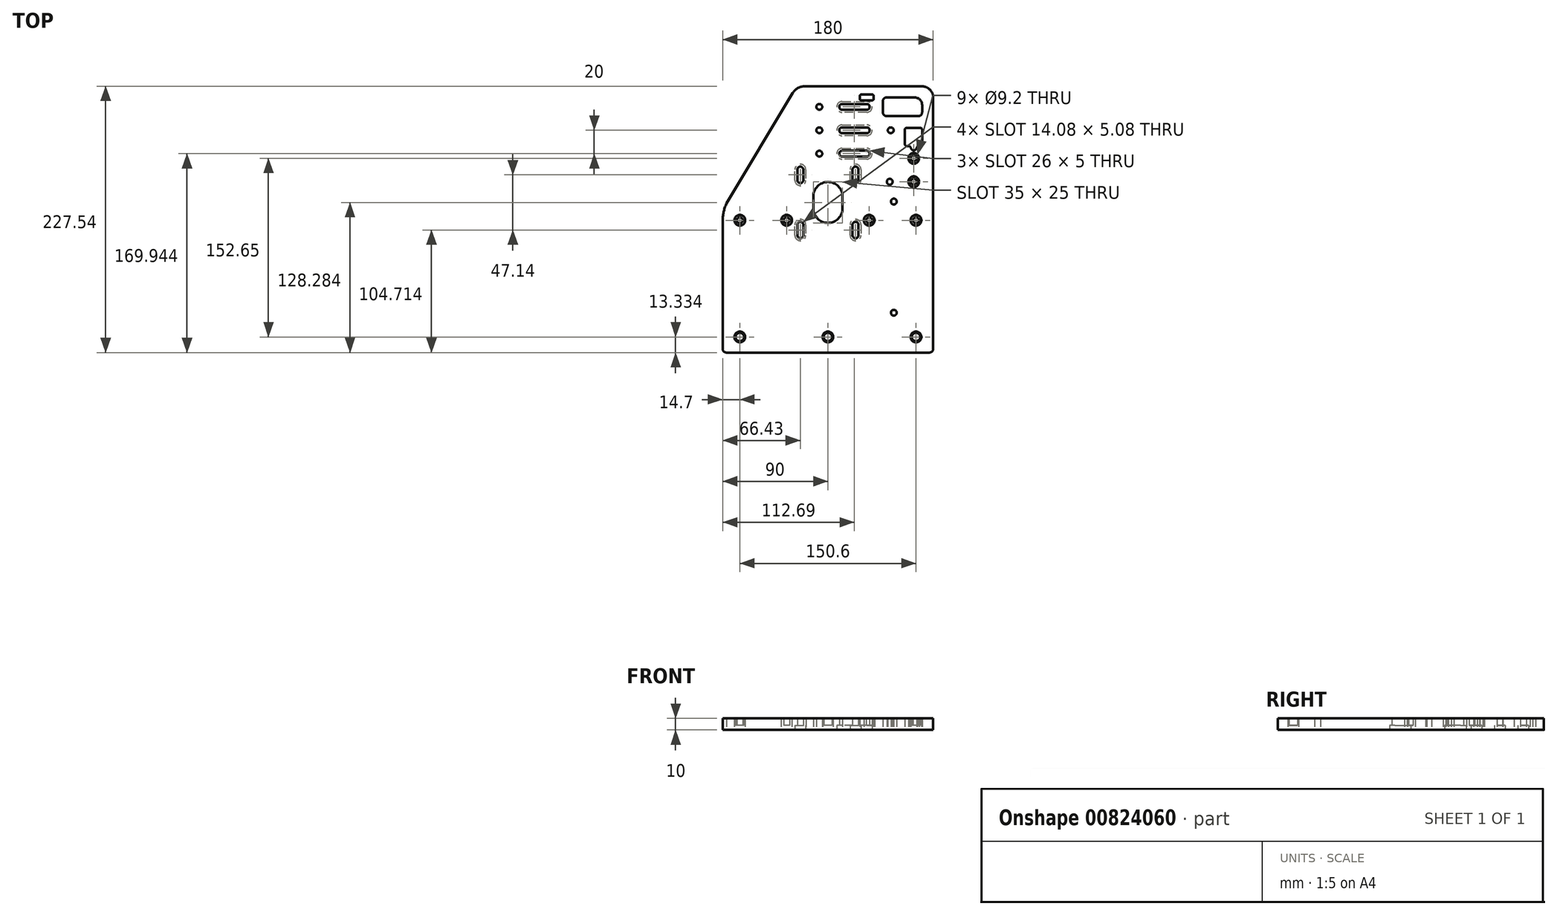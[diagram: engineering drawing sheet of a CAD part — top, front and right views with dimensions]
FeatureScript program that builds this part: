
annotation { "Feature Type Name" : "Feature", "Feature Type Description" : "" }
export const myFeature = defineFeature(function(context is Context, id is Id, definition is map)
    precondition{}
    {
        {
            var Q0;
            Q0=qCreatedBy(makeId("Top.planeOp"),FACE);
            var sketch = newSketch(context, id + "F0", { "sketchPlane" : qUnion([Q0])});
            skLineSegment(sketch, "E0", {"start": v(-86.67, -113.77) * mm, "end": v(86.64, -113.77) * mm});
            skLineSegment(sketch, "E1", {"start": v(-90, -1.46) * mm, "end": v(-90, -110.4) * mm});
            skLineSegment(sketch, "E2", {"start": v(-30.03, 107.94) * mm, "end": v(-86.68, 13.65) * mm});
            skLineSegment(sketch, "E3", {"start": v(-26.11, -13.56) * mm, "end": v(-26.11, -4.56) * mm});
            skLineSegment(sketch, "E4", {"start": v(-26.11, 33.58) * mm, "end": v(-26.11, 42.58) * mm});
            skLineSegment(sketch, "E5", {"start": v(-21.03, 42.58) * mm, "end": v(-21.03, 33.58) * mm});
            skLineSegment(sketch, "E6", {"start": v(-21.03, -4.56) * mm, "end": v(-21.03, -13.56) * mm});
            skLineSegment(sketch, "E7", {"start": v(-12.5, 9.51) * mm, "end": v(-12.5, 19.51) * mm});
            skLineSegment(sketch, "E8", {"start": v(12.5, 19.51) * mm, "end": v(12.5, 9.51) * mm});
            skLineSegment(sketch, "E9", {"start": v(21.03, -13.56) * mm, "end": v(21.03, -4.56) * mm});
            skLineSegment(sketch, "E10", {"start": v(21.03, 33.58) * mm, "end": v(21.03, 42.58) * mm});
            skLineSegment(sketch, "E11", {"start": v(26.1, 42.58) * mm, "end": v(26.1, 33.58) * mm});
            skLineSegment(sketch, "E12", {"start": v(26.1, -4.56) * mm, "end": v(26.1, -13.56) * mm});
            skLineSegment(sketch, "E13", {"start": v(27.19, 103.2) * mm, "end": v(27.19, 105.32) * mm});
            skLineSegment(sketch, "E14", {"start": v(76.37, 62.2) * mm, "end": v(75.8, 61.48) * mm});
            skLineSegment(sketch, "E15", {"start": v(39.19, 105.32) * mm, "end": v(39.19, 103.2) * mm});
            skLineSegment(sketch, "E16", {"start": v(47, 91.4) * mm, "end": v(47, 101.1) * mm});
            skLineSegment(sketch, "E17", {"start": v(33.19, 53.67) * mm, "end": v(12.19, 53.67) * mm});
            skLineSegment(sketch, "E18", {"start": v(12.19, 58.67) * mm, "end": v(33.19, 58.67) * mm});
            skLineSegment(sketch, "E19", {"start": v(65.8, 64.35) * mm, "end": v(65.8, 76.68) * mm});
            skLineSegment(sketch, "E20", {"start": v(78.84, 62.2) * mm, "end": v(76.37, 62.2) * mm});
            skLineSegment(sketch, "E21", {"start": v(69.93, 62.7) * mm, "end": v(67.46, 62.7) * mm});
            skLineSegment(sketch, "E22", {"start": v(33.19, 73.67) * mm, "end": v(12.19, 73.67) * mm});
            skLineSegment(sketch, "E23", {"start": v(67.46, 78.34) * mm, "end": v(78.84, 78.34) * mm});
            skLineSegment(sketch, "E24", {"start": v(80.5, 97.88) * mm, "end": v(80.5, 91.4) * mm});
            skLineSegment(sketch, "E25", {"start": v(80.5, 76.68) * mm, "end": v(80.5, 63.85) * mm});
            skLineSegment(sketch, "E26", {"start": v(12.19, 78.67) * mm, "end": v(33.19, 78.67) * mm});
            skLineSegment(sketch, "E27", {"start": v(77.36, 88.26) * mm, "end": v(50.14, 88.26) * mm});
            skLineSegment(sketch, "E28", {"start": v(90, -110.4) * mm, "end": v(90, 104.05) * mm});
            skLineSegment(sketch, "E29", {"start": v(33.19, 93.67) * mm, "end": v(12.19, 93.67) * mm});
            skLineSegment(sketch, "E30", {"start": v(70.9, 61.48) * mm, "end": v(69.93, 62.7) * mm});
            skLineSegment(sketch, "E31", {"start": v(12.19, 98.67) * mm, "end": v(33.19, 98.67) * mm});
            skLineSegment(sketch, "E32", {"start": v(37.75, 101.76) * mm, "end": v(28.63, 101.76) * mm});
            skLineSegment(sketch, "E33", {"start": v(50.14, 104.23) * mm, "end": v(74.15, 104.23) * mm});
            skLineSegment(sketch, "E34", {"start": v(28.63, 106.76) * mm, "end": v(37.75, 106.76) * mm});
            skLineSegment(sketch, "E35", {"start": v(80.33, 113.73) * mm, "end": v(-18.85, 113.73) * mm});
            skCircle(sketch, "E36", {"center": v(-75.3, -100.44) * mm, "radius": 3.6 * mm});
            skArc(sketch, "E37", {"start": v(-90, -110.4) * mm, "mid": v(-89.03, -112.77) * mm, "end": v(-86.67, -113.77) * mm});
            skArc(sketch, "E38", {"start": v(-26.11, -13.56) * mm, "mid": v(-23.57, -16.1) * mm, "end": v(-21.03, -13.56) * mm});
            skArc(sketch, "E39", {"start": v(-21.03, -4.56) * mm, "mid": v(-23.57, -2.02) * mm, "end": v(-26.11, -4.56) * mm});
            skArc(sketch, "E40", {"start": v(-86.68, 13.65) * mm, "mid": v(-89.16, 6.28) * mm, "end": v(-90, -1.46) * mm});
            skArc(sketch, "E41", {"start": v(-18.85, 113.73) * mm, "mid": v(-25.26, 112.42) * mm, "end": v(-30.03, 107.94) * mm});
            skArc(sketch, "E42", {"start": v(-21.03, 42.58) * mm, "mid": v(-23.57, 45.12) * mm, "end": v(-26.11, 42.58) * mm});
            skArc(sketch, "E43", {"start": v(-26.11, 33.58) * mm, "mid": v(-23.57, 31.04) * mm, "end": v(-21.03, 33.58) * mm});
            skCircle(sketch, "E44", {"center": v(-7.31, 96.17) * mm, "radius": 2.5 * mm});
            skCircle(sketch, "E45", {"center": v(-7.31, 76.17) * mm, "radius": 2.5 * mm});
            skCircle(sketch, "E46", {"center": v(-7.31, 56.17) * mm, "radius": 2.5 * mm});
            skCircle(sketch, "E47", {"center": v(-35.3, -0.74) * mm, "radius": 2.5 * mm});
            skCircle(sketch, "E48", {"center": v(-75.3, -0.74) * mm, "radius": 2.5 * mm});
            skCircle(sketch, "E49", {"center": v(75.3, -100.44) * mm, "radius": 3.6 * mm});
            skCircle(sketch, "E50", {"center": v(0, -100.44) * mm, "radius": 3.6 * mm});
            skArc(sketch, "E51", {"start": v(86.64, -113.77) * mm, "mid": v(89.02, -112.78) * mm, "end": v(90, -110.4) * mm});
            skArc(sketch, "E52", {"start": v(21.03, -13.56) * mm, "mid": v(23.57, -16.1) * mm, "end": v(26.1, -13.56) * mm});
            skArc(sketch, "E53", {"start": v(26.1, -4.56) * mm, "mid": v(23.57, -2.02) * mm, "end": v(21.03, -4.56) * mm});
            skCircle(sketch, "E54", {"center": v(56.34, -79.74) * mm, "radius": 2.5 * mm});
            skArc(sketch, "E55", {"start": v(-12.5, 9.51) * mm, "mid": v(0, -2.99) * mm, "end": v(12.5, 9.51) * mm});
            skArc(sketch, "E56", {"start": v(12.5, 19.51) * mm, "mid": v(0, 32.01) * mm, "end": v(-12.5, 19.51) * mm});
            skArc(sketch, "E57", {"start": v(90, 104.05) * mm, "mid": v(87.17, 110.9) * mm, "end": v(80.33, 113.73) * mm});
            skArc(sketch, "E58", {"start": v(80.5, 97.88) * mm, "mid": v(78.64, 102.37) * mm, "end": v(74.15, 104.23) * mm});
            skArc(sketch, "E59", {"start": v(77.36, 88.26) * mm, "mid": v(79.58, 89.18) * mm, "end": v(80.5, 91.4) * mm});
            skArc(sketch, "E60", {"start": v(47, 91.4) * mm, "mid": v(47.92, 89.18) * mm, "end": v(50.14, 88.26) * mm});
            skArc(sketch, "E61", {"start": v(50.14, 104.23) * mm, "mid": v(47.92, 103.31) * mm, "end": v(47, 101.1) * mm});
            skArc(sketch, "E62", {"start": v(21.03, 33.58) * mm, "mid": v(23.57, 31.04) * mm, "end": v(26.1, 33.58) * mm});
            skArc(sketch, "E63", {"start": v(26.1, 42.58) * mm, "mid": v(23.57, 45.12) * mm, "end": v(21.03, 42.58) * mm});
            skArc(sketch, "E64", {"start": v(33.19, 93.67) * mm, "mid": v(35.69, 96.17) * mm, "end": v(33.19, 98.67) * mm});
            skArc(sketch, "E65", {"start": v(12.19, 98.67) * mm, "mid": v(9.69, 96.17) * mm, "end": v(12.19, 93.67) * mm});
            skArc(sketch, "E66", {"start": v(33.19, 73.67) * mm, "mid": v(35.69, 76.17) * mm, "end": v(33.19, 78.67) * mm});
            skArc(sketch, "E67", {"start": v(12.19, 78.67) * mm, "mid": v(9.69, 76.17) * mm, "end": v(12.19, 73.67) * mm});
            skArc(sketch, "E68", {"start": v(33.19, 53.67) * mm, "mid": v(35.69, 56.17) * mm, "end": v(33.19, 58.67) * mm});
            skArc(sketch, "E69", {"start": v(12.19, 58.67) * mm, "mid": v(9.69, 56.17) * mm, "end": v(12.19, 53.67) * mm});
            skCircle(sketch, "E70", {"center": v(53.69, 76.17) * mm, "radius": 2.5 * mm});
            skCircle(sketch, "E71", {"center": v(73.35, 52.21) * mm, "radius": 2.5 * mm});
            skCircle(sketch, "E72", {"center": v(73.35, 32.21) * mm, "radius": 2.5 * mm});
            skCircle(sketch, "E73", {"center": v(52.85, 32.21) * mm, "radius": 2.5 * mm});
            skCircle(sketch, "E74", {"center": v(56.34, 15.26) * mm, "radius": 2.5 * mm});
            skCircle(sketch, "E75", {"center": v(75.3, -0.74) * mm, "radius": 2.5 * mm});
            skCircle(sketch, "E76", {"center": v(35.3, -0.74) * mm, "radius": 2.5 * mm});
            skArc(sketch, "E77", {"start": v(80.5, 76.68) * mm, "mid": v(80.01, 77.86) * mm, "end": v(78.84, 78.34) * mm});
            skArc(sketch, "E78", {"start": v(78.84, 62.2) * mm, "mid": v(80.01, 62.68) * mm, "end": v(80.5, 63.85) * mm});
            skArc(sketch, "E79", {"start": v(65.8, 64.35) * mm, "mid": v(66.29, 63.18) * mm, "end": v(67.46, 62.7) * mm});
            skArc(sketch, "E80", {"start": v(67.46, 78.34) * mm, "mid": v(66.29, 77.86) * mm, "end": v(65.8, 76.68) * mm});
            skArc(sketch, "E81", {"start": v(39.19, 105.32) * mm, "mid": v(38.77, 106.34) * mm, "end": v(37.75, 106.76) * mm});
            skArc(sketch, "E82", {"start": v(37.75, 101.76) * mm, "mid": v(38.77, 102.19) * mm, "end": v(39.19, 103.2) * mm});
            skArc(sketch, "E83", {"start": v(27.19, 103.2) * mm, "mid": v(27.61, 102.19) * mm, "end": v(28.63, 101.76) * mm});
            skArc(sketch, "E84", {"start": v(28.63, 106.76) * mm, "mid": v(27.61, 106.34) * mm, "end": v(27.19, 105.32) * mm});
            skEllipticalArc(sketch, "E85", {});
            skArc(sketch, "E86.0", {"start": v(-28.21, -13.56) * mm, "mid": v(-23.57, -18.2) * mm, "end": v(-18.93, -13.56) * mm});
            skLineSegment(sketch, "E86.1", {"start": v(-28.21, -13.56) * mm, "end": v(-28.21, -4.56) * mm});
            skArc(sketch, "E86.2", {"start": v(-18.93, -4.56) * mm, "mid": v(-23.57, 0.08) * mm, "end": v(-28.21, -4.56) * mm});
            skLineSegment(sketch, "E86.3", {"start": v(-18.93, -4.56) * mm, "end": v(-18.93, -13.56) * mm});
            skArc(sketch, "E87.0", {"start": v(-18.93, 42.58) * mm, "mid": v(-23.57, 47.22) * mm, "end": v(-28.21, 42.58) * mm});
            skLineSegment(sketch, "E87.1", {"start": v(-18.93, 42.58) * mm, "end": v(-18.93, 33.58) * mm});
            skArc(sketch, "E87.2", {"start": v(-28.21, 33.58) * mm, "mid": v(-23.57, 28.94) * mm, "end": v(-18.93, 33.58) * mm});
            skLineSegment(sketch, "E87.3", {"start": v(-28.21, 33.58) * mm, "end": v(-28.21, 42.58) * mm});
            skArc(sketch, "E88.0", {"start": v(18.93, 33.58) * mm, "mid": v(23.57, 28.94) * mm, "end": v(28.2, 33.58) * mm});
            skLineSegment(sketch, "E88.1", {"start": v(18.93, 33.58) * mm, "end": v(18.93, 42.58) * mm});
            skArc(sketch, "E88.2", {"start": v(28.2, 42.58) * mm, "mid": v(23.57, 47.22) * mm, "end": v(18.93, 42.58) * mm});
            skLineSegment(sketch, "E88.3", {"start": v(28.2, 42.58) * mm, "end": v(28.2, 33.58) * mm});
            skArc(sketch, "E89.0", {"start": v(28.2, -4.56) * mm, "mid": v(23.57, 0.08) * mm, "end": v(18.93, -4.56) * mm});
            skLineSegment(sketch, "E89.1", {"start": v(28.2, -4.56) * mm, "end": v(28.2, -13.56) * mm});
            skArc(sketch, "E89.2", {"start": v(18.93, -13.56) * mm, "mid": v(23.57, -18.2) * mm, "end": v(28.2, -13.56) * mm});
            skLineSegment(sketch, "E89.3", {"start": v(18.93, -13.56) * mm, "end": v(18.93, -4.56) * mm});
            skCircle(sketch, "E90.0", {"center": v(-75.3, -100.44) * mm, "radius": 4.6 * mm});
            skCircle(sketch, "E91.0", {"center": v(0, -100.44) * mm, "radius": 4.6 * mm});
            skCircle(sketch, "E92.0", {"center": v(75.3, -100.44) * mm, "radius": 4.6 * mm});
            skCircle(sketch, "E93.0", {"center": v(75.3, -0.74) * mm, "radius": 4.6 * mm});
            skCircle(sketch, "E94.0", {"center": v(35.3, -0.74) * mm, "radius": 4.6 * mm});
            skCircle(sketch, "E95.0", {"center": v(-35.3, -0.74) * mm, "radius": 4.6 * mm});
            skCircle(sketch, "E96.0", {"center": v(-75.3, -0.74) * mm, "radius": 4.6 * mm});
            skArc(sketch, "E97.0", {"start": v(12.19, 100.77) * mm, "mid": v(7.59, 96.17) * mm, "end": v(12.19, 91.57) * mm});
            skLineSegment(sketch, "E97.1", {"start": v(12.19, 100.77) * mm, "end": v(33.19, 100.77) * mm});
            skArc(sketch, "E97.2", {"start": v(33.19, 91.57) * mm, "mid": v(37.79, 96.17) * mm, "end": v(33.19, 100.77) * mm});
            skLineSegment(sketch, "E97.3", {"start": v(33.19, 91.57) * mm, "end": v(12.19, 91.57) * mm});
            skLineSegment(sketch, "E98.0", {"start": v(12.19, 80.77) * mm, "end": v(33.19, 80.77) * mm});
            skArc(sketch, "E98.1", {"start": v(12.19, 80.77) * mm, "mid": v(7.59, 76.17) * mm, "end": v(12.19, 71.57) * mm});
            skLineSegment(sketch, "E98.2", {"start": v(33.19, 71.57) * mm, "end": v(12.19, 71.57) * mm});
            skArc(sketch, "E98.3", {"start": v(33.19, 71.57) * mm, "mid": v(37.79, 76.17) * mm, "end": v(33.19, 80.77) * mm});
            skLineSegment(sketch, "E99.0", {"start": v(12.19, 60.77) * mm, "end": v(33.19, 60.77) * mm});
            skArc(sketch, "E99.1", {"start": v(12.19, 60.77) * mm, "mid": v(7.59, 56.17) * mm, "end": v(12.19, 51.57) * mm});
            skLineSegment(sketch, "E99.2", {"start": v(33.19, 51.57) * mm, "end": v(12.19, 51.57) * mm});
            skArc(sketch, "E99.3", {"start": v(33.19, 51.57) * mm, "mid": v(37.79, 56.17) * mm, "end": v(33.19, 60.77) * mm});
            skCircle(sketch, "E100.0", {"center": v(73.35, 52.21) * mm, "radius": 4.6 * mm});
            skCircle(sketch, "E101.0", {"center": v(73.35, 32.21) * mm, "radius": 4.6 * mm});
            const initialGuessF0  = {"E85": [0.073349997, 0.06148353900000001, 2.452987, 0, 0.002452987, 0.002452987, -3.141593, 0]};
            skSetInitialGuess(sketch, initialGuessF0);
            skSolve(sketch);
        }
        {
            var Q0;
            Q0=qSketchRegion(id+"F0",true);
            var Q1;
            Q1=makeQuery(id+"F0.imprint","IMPRINT",FACE,{"disambiguationData":[TD([[makeQuery(id+"F0.imprint","IMPRINT",EDGE,{"derivedFrom":sQuery(id+"F0.wireOp",EDGE,"E48")}),1.0]])]});
            var Q2;
            Q2=makeQuery(id+"F0.imprint","IMPRINT",FACE,{"disambiguationData":[TD([[makeQuery(id+"F0.imprint","IMPRINT",EDGE,{"derivedFrom":sQuery(id+"F0.wireOp",EDGE,"E47")}),1.0]])]});
            var Q3;
            Q3=makeQuery(id+"F0.imprint","IMPRINT",FACE,{"disambiguationData":[TD([[makeQuery(id+"F0.imprint","IMPRINT",EDGE,{"derivedFrom":sQuery(id+"F0.wireOp",EDGE,"E3")}),1.0]])]});
            var Q4;
            Q4=makeQuery(id+"F0.imprint","IMPRINT",FACE,{"disambiguationData":[TD([[makeQuery(id+"F0.imprint","IMPRINT",EDGE,{"derivedFrom":sQuery(id+"F0.wireOp",EDGE,"E4")}),1.0]])]});
            var Q5;
            Q5=makeQuery(id+"F0.imprint","IMPRINT",FACE,{"disambiguationData":[TD([[makeQuery(id+"F0.imprint","IMPRINT",EDGE,{"derivedFrom":sQuery(id+"F0.wireOp",EDGE,"E10")}),1.0]])]});
            var Q6;
            Q6=makeQuery(id+"F0.imprint","IMPRINT",FACE,{"disambiguationData":[TD([[makeQuery(id+"F0.imprint","IMPRINT",EDGE,{"derivedFrom":sQuery(id+"F0.wireOp",EDGE,"E9")}),1.0]])]});
            var Q7;
            Q7=makeQuery(id+"F0.imprint","IMPRINT",FACE,{"disambiguationData":[TD([[makeQuery(id+"F0.imprint","IMPRINT",EDGE,{"derivedFrom":sQuery(id+"F0.wireOp",EDGE,"E76")}),1.0]])]});
            var Q8;
            Q8=makeQuery(id+"F0.imprint","IMPRINT",FACE,{"disambiguationData":[TD([[makeQuery(id+"F0.imprint","IMPRINT",EDGE,{"derivedFrom":sQuery(id+"F0.wireOp",EDGE,"E75")}),1.0]])]});
            var Q9;
            Q9=makeQuery(id+"F0.imprint","IMPRINT",FACE,{"disambiguationData":[TD([[makeQuery(id+"F0.imprint","IMPRINT",EDGE,{"derivedFrom":sQuery(id+"F0.wireOp",EDGE,"E36")}),1.0]])]});
            var Q10;
            Q10=makeQuery(id+"F0.imprint","IMPRINT",FACE,{"disambiguationData":[TD([[makeQuery(id+"F0.imprint","IMPRINT",EDGE,{"derivedFrom":sQuery(id+"F0.wireOp",EDGE,"E50")}),1.0]])]});
            var Q11;
            Q11=makeQuery(id+"F0.imprint","IMPRINT",FACE,{"disambiguationData":[TD([[makeQuery(id+"F0.imprint","IMPRINT",EDGE,{"derivedFrom":sQuery(id+"F0.wireOp",EDGE,"E49")}),1.0]])]});
            var Q12;
            Q12=makeQuery(id+"F0.imprint","IMPRINT",FACE,{"disambiguationData":[TD([[makeQuery(id+"F0.imprint","IMPRINT",EDGE,{"derivedFrom":sQuery(id+"F0.wireOp",EDGE,"E17")}),1.0]])]});
            var Q13;
            Q13=makeQuery(id+"F0.imprint","IMPRINT",FACE,{"disambiguationData":[TD([[makeQuery(id+"F0.imprint","IMPRINT",EDGE,{"derivedFrom":sQuery(id+"F0.wireOp",EDGE,"E22")}),1.0]])]});
            var Q14;
            Q14=makeQuery(id+"F0.imprint","IMPRINT",FACE,{"disambiguationData":[TD([[makeQuery(id+"F0.imprint","IMPRINT",EDGE,{"derivedFrom":sQuery(id+"F0.wireOp",EDGE,"E29")}),1.0]])]});
            var Q15;
            Q15=makeQuery(id+"F0.imprint","IMPRINT",FACE,{"disambiguationData":[TD([[makeQuery(id+"F0.imprint","IMPRINT",EDGE,{"derivedFrom":sQuery(id+"F0.wireOp",EDGE,"E72")}),1.0]])]});
            var Q16;
            Q16=makeQuery(id+"F0.imprint","IMPRINT",FACE,{"disambiguationData":[TD([[makeQuery(id+"F0.imprint","IMPRINT",EDGE,{"derivedFrom":sQuery(id+"F0.wireOp",EDGE,"E71")}),1.0]])]});
            extrude(context, id + "F1", {"entities" : qUnion([Q0, Q1, Q2, Q3, Q4, Q5, Q6, Q7, Q8, Q9, Q10, Q11, Q12, Q13, Q14, Q15, Q16]), "depth" : 10 * mm, "offsetDistance" : 25 * mm});
        }
        {
            var Q0;
            Q0=makeQuery(id+"F0.imprint","IMPRINT",FACE,{"disambiguationData":[TD([[makeQuery(id+"F0.imprint","IMPRINT",EDGE,{"derivedFrom":sQuery(id+"F0.wireOp",EDGE,"E36")}),1.0]])]});
            var Q1;
            Q1=makeQuery(id+"F0.imprint","IMPRINT",FACE,{"disambiguationData":[TD([[makeQuery(id+"F0.imprint","IMPRINT",EDGE,{"derivedFrom":sQuery(id+"F0.wireOp",EDGE,"E50")}),1.0]])]});
            var Q2;
            Q2=makeQuery(id+"F0.imprint","IMPRINT",FACE,{"disambiguationData":[TD([[makeQuery(id+"F0.imprint","IMPRINT",EDGE,{"derivedFrom":sQuery(id+"F0.wireOp",EDGE,"E49")}),1.0]])]});
            var Q3;
            Q3=makeQuery(id+"F0.imprint","IMPRINT",FACE,{"disambiguationData":[TD([[makeQuery(id+"F0.imprint","IMPRINT",EDGE,{"derivedFrom":sQuery(id+"F0.wireOp",EDGE,"E3")}),1.0]])]});
            var Q4;
            Q4=makeQuery(id+"F0.imprint","IMPRINT",FACE,{"disambiguationData":[TD([[makeQuery(id+"F0.imprint","IMPRINT",EDGE,{"derivedFrom":sQuery(id+"F0.wireOp",EDGE,"E9")}),1.0]])]});
            var Q5;
            Q5=makeQuery(id+"F0.imprint","IMPRINT",FACE,{"disambiguationData":[TD([[makeQuery(id+"F0.imprint","IMPRINT",EDGE,{"derivedFrom":sQuery(id+"F0.wireOp",EDGE,"E4")}),1.0]])]});
            var Q6;
            Q6=makeQuery(id+"F0.imprint","IMPRINT",FACE,{"disambiguationData":[TD([[makeQuery(id+"F0.imprint","IMPRINT",EDGE,{"derivedFrom":sQuery(id+"F0.wireOp",EDGE,"E10")}),1.0]])]});
            var Q7;
            Q7=makeQuery(id+"F0.imprint","IMPRINT",FACE,{"disambiguationData":[TD([[makeQuery(id+"F0.imprint","IMPRINT",EDGE,{"derivedFrom":sQuery(id+"F0.wireOp",EDGE,"E48")}),1.0]])]});
            var Q8;
            Q8=makeQuery(id+"F0.imprint","IMPRINT",FACE,{"disambiguationData":[TD([[makeQuery(id+"F0.imprint","IMPRINT",EDGE,{"derivedFrom":sQuery(id+"F0.wireOp",EDGE,"E76")}),1.0]])]});
            var Q9;
            Q9=makeQuery(id+"F0.imprint","IMPRINT",FACE,{"disambiguationData":[TD([[makeQuery(id+"F0.imprint","IMPRINT",EDGE,{"derivedFrom":sQuery(id+"F0.wireOp",EDGE,"E47")}),1.0]])]});
            var Q10;
            Q10=makeQuery(id+"F0.imprint","IMPRINT",FACE,{"disambiguationData":[TD([[makeQuery(id+"F0.imprint","IMPRINT",EDGE,{"derivedFrom":sQuery(id+"F0.wireOp",EDGE,"E75")}),1.0]])]});
            var Q11;
            Q11=makeQuery(id+"F0.imprint","IMPRINT",FACE,{"disambiguationData":[TD([[makeQuery(id+"F0.imprint","IMPRINT",EDGE,{"derivedFrom":sQuery(id+"F0.wireOp",EDGE,"E72")}),1.0]])]});
            var Q12;
            Q12=makeQuery(id+"F0.imprint","IMPRINT",FACE,{"disambiguationData":[TD([[makeQuery(id+"F0.imprint","IMPRINT",EDGE,{"derivedFrom":sQuery(id+"F0.wireOp",EDGE,"E71")}),1.0]])]});
            var Q13;
            Q13=makeQuery(id+"F0.imprint","IMPRINT",FACE,{"disambiguationData":[TD([[makeQuery(id+"F0.imprint","IMPRINT",EDGE,{"derivedFrom":sQuery(id+"F0.wireOp",EDGE,"E17")}),1.0]])]});
            var Q14;
            Q14=makeQuery(id+"F0.imprint","IMPRINT",FACE,{"disambiguationData":[TD([[makeQuery(id+"F0.imprint","IMPRINT",EDGE,{"derivedFrom":sQuery(id+"F0.wireOp",EDGE,"E22")}),1.0]])]});
            var Q15;
            Q15=makeQuery(id+"F0.imprint","IMPRINT",FACE,{"disambiguationData":[TD([[makeQuery(id+"F0.imprint","IMPRINT",EDGE,{"derivedFrom":sQuery(id+"F0.wireOp",EDGE,"E29")}),1.0]])]});
            var Q16;
            Q16=makeQuery(id+"F1.opExtrude","CAP_FACE",FACE,{"disambiguationData":[OSD([sQuery(id+"F0.wireOp",EDGE,"E0"),sQuery(id+"F0.wireOp",EDGE,"E1"),sQuery(id+"F0.wireOp",EDGE,"E2"),sQuery(id+"F0.wireOp",EDGE,"E3"),sQuery(id+"F0.wireOp",EDGE,"E4"),sQuery(id+"F0.wireOp",EDGE,"E5"),sQuery(id+"F0.wireOp",EDGE,"E6"),sQuery(id+"F0.wireOp",EDGE,"E7"),sQuery(id+"F0.wireOp",EDGE,"E8"),sQuery(id+"F0.wireOp",EDGE,"E9"),sQuery(id+"F0.wireOp",EDGE,"E10"),sQuery(id+"F0.wireOp",EDGE,"E11"),sQuery(id+"F0.wireOp",EDGE,"E12"),sQuery(id+"F0.wireOp",EDGE,"E13"),sQuery(id+"F0.wireOp",EDGE,"E14"),sQuery(id+"F0.wireOp",EDGE,"E15"),sQuery(id+"F0.wireOp",EDGE,"E16"),sQuery(id+"F0.wireOp",EDGE,"E17"),sQuery(id+"F0.wireOp",EDGE,"E18"),sQuery(id+"F0.wireOp",EDGE,"E19"),sQuery(id+"F0.wireOp",EDGE,"E20"),sQuery(id+"F0.wireOp",EDGE,"E21"),sQuery(id+"F0.wireOp",EDGE,"E22"),sQuery(id+"F0.wireOp",EDGE,"E23"),sQuery(id+"F0.wireOp",EDGE,"E24"),sQuery(id+"F0.wireOp",EDGE,"E25"),sQuery(id+"F0.wireOp",EDGE,"E26"),sQuery(id+"F0.wireOp",EDGE,"E27"),sQuery(id+"F0.wireOp",EDGE,"E28"),sQuery(id+"F0.wireOp",EDGE,"E29"),sQuery(id+"F0.wireOp",EDGE,"E30"),sQuery(id+"F0.wireOp",EDGE,"E31"),sQuery(id+"F0.wireOp",EDGE,"E32"),sQuery(id+"F0.wireOp",EDGE,"E33"),sQuery(id+"F0.wireOp",EDGE,"E34"),sQuery(id+"F0.wireOp",EDGE,"E35"),sQuery(id+"F0.wireOp",EDGE,"E36"),sQuery(id+"F0.wireOp",EDGE,"E37"),sQuery(id+"F0.wireOp",EDGE,"E38"),sQuery(id+"F0.wireOp",EDGE,"E39"),sQuery(id+"F0.wireOp",EDGE,"E40"),sQuery(id+"F0.wireOp",EDGE,"E41"),sQuery(id+"F0.wireOp",EDGE,"E42"),sQuery(id+"F0.wireOp",EDGE,"E43"),sQuery(id+"F0.wireOp",EDGE,"E44"),sQuery(id+"F0.wireOp",EDGE,"E45"),sQuery(id+"F0.wireOp",EDGE,"E46"),sQuery(id+"F0.wireOp",EDGE,"E47"),sQuery(id+"F0.wireOp",EDGE,"E48"),sQuery(id+"F0.wireOp",EDGE,"E49"),sQuery(id+"F0.wireOp",EDGE,"E50"),sQuery(id+"F0.wireOp",EDGE,"E51"),sQuery(id+"F0.wireOp",EDGE,"E52"),sQuery(id+"F0.wireOp",EDGE,"E53"),sQuery(id+"F0.wireOp",EDGE,"E54"),sQuery(id+"F0.wireOp",EDGE,"E55"),sQuery(id+"F0.wireOp",EDGE,"E56"),sQuery(id+"F0.wireOp",EDGE,"E57"),sQuery(id+"F0.wireOp",EDGE,"E58"),sQuery(id+"F0.wireOp",EDGE,"E59"),sQuery(id+"F0.wireOp",EDGE,"E60"),sQuery(id+"F0.wireOp",EDGE,"E61"),sQuery(id+"F0.wireOp",EDGE,"E62"),sQuery(id+"F0.wireOp",EDGE,"E63"),sQuery(id+"F0.wireOp",EDGE,"E64"),sQuery(id+"F0.wireOp",EDGE,"E65"),sQuery(id+"F0.wireOp",EDGE,"E66"),sQuery(id+"F0.wireOp",EDGE,"E67"),sQuery(id+"F0.wireOp",EDGE,"E68"),sQuery(id+"F0.wireOp",EDGE,"E69"),sQuery(id+"F0.wireOp",EDGE,"E70"),sQuery(id+"F0.wireOp",EDGE,"E71"),sQuery(id+"F0.wireOp",EDGE,"E72"),sQuery(id+"F0.wireOp",EDGE,"E73"),sQuery(id+"F0.wireOp",EDGE,"E74"),sQuery(id+"F0.wireOp",EDGE,"E75"),sQuery(id+"F0.wireOp",EDGE,"E76"),sQuery(id+"F0.wireOp",EDGE,"E77"),sQuery(id+"F0.wireOp",EDGE,"E78"),sQuery(id+"F0.wireOp",EDGE,"E79"),sQuery(id+"F0.wireOp",EDGE,"E80"),sQuery(id+"F0.wireOp",EDGE,"E81"),sQuery(id+"F0.wireOp",EDGE,"E82"),sQuery(id+"F0.wireOp",EDGE,"E83"),sQuery(id+"F0.wireOp",EDGE,"E84"),sQuery(id+"F0.wireOp",EDGE,"E85")])],"isStart":false});
            extrude(context, id + "F2", {"entities" : qUnion([Q0, Q1, Q2, Q3, Q4, Q5, Q6, Q7, Q8, Q9, Q10, Q11, Q12, Q13, Q14, Q15]), "operationType" : NewBodyOperationType.REMOVE, "endBound" : BoundingType.UP_TO_SURFACE, "depth" : 6 * mm, "endBoundEntityFace" : qUnion([Q16]), "hasOffset" : true, "offsetDistance" : 6 * mm});
        }
    });
